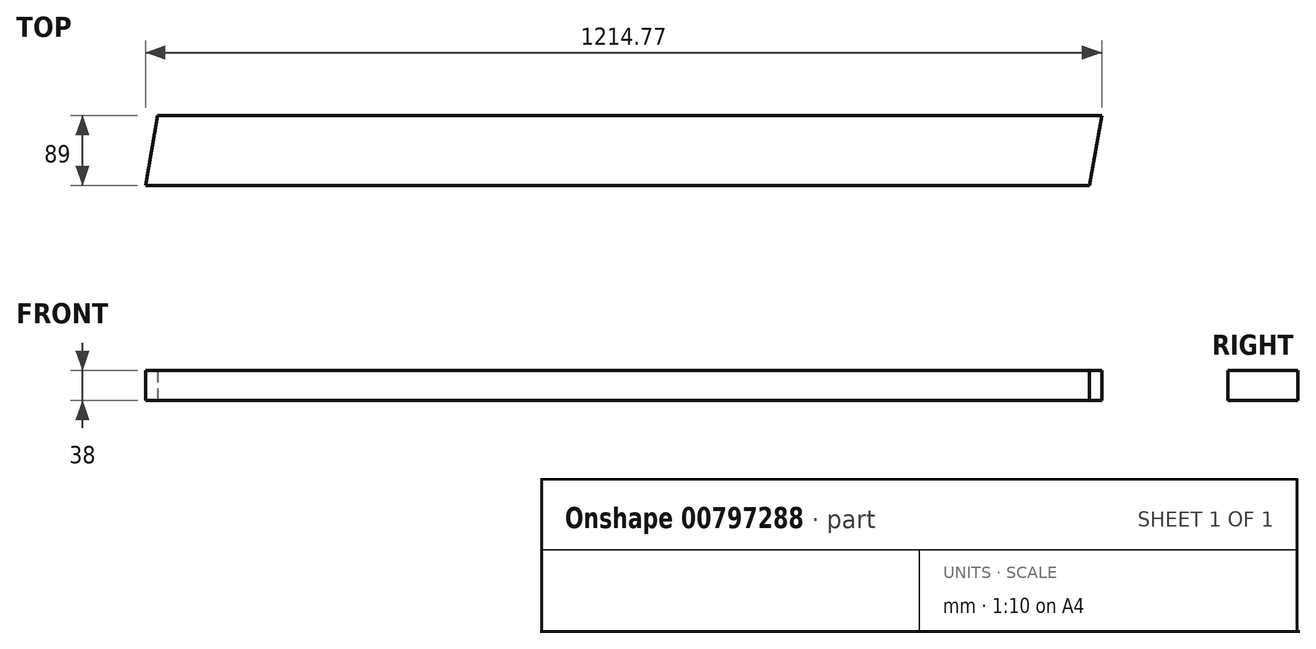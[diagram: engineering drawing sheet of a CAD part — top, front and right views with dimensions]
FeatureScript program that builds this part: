
annotation { "Feature Type Name" : "Feature", "Feature Type Description" : "" }
export const myFeature = defineFeature(function(context is Context, id is Id, definition is map)
    precondition{}
    {
        {
            var Q0;
            Q0=qCreatedBy(makeId("Top.planeOp"),FACE);
            var sketch = newSketch(context, id + "F0", { "sketchPlane" : qUnion([Q0])});
            skLineSegment(sketch, "E0.bottom", {"start": v(464.77, 44.5) * mm, "end": v(-734.3, 44.5) * mm});
            skLineSegment(sketch, "E0.top", {"start": v(449.07, -44.5) * mm, "end": v(-750, -44.5) * mm});
            skPoint(sketch, "E0.middle", {"position": v(0, 0) * mm});
            skLineSegment(sketch, "E1", {"start": v(449.07, -44.5) * mm, "end": v(464.77, 44.5) * mm});
            skLineSegment(sketch, "E2", {"start": v(-750, -44.5) * mm, "end": v(-734.3, 44.5) * mm});
            skPoint(sketch, "E0.left.start.orphan", {"position": v(750, 44.5) * mm});
            skPoint(sketch, "E0.right.start.orphan", {"position": v(-449.07, 44.5) * mm});
            skSolve(sketch);
        }
        {
            var Q0;
            Q0=qSketchRegion(id+"F0",true);
            extrude(context, id + "F1", {"entities" : qUnion([Q0]), "depth" : 38 * mm, "offsetDistance" : 25 * mm, "symmetric" : true});
        }
    });
